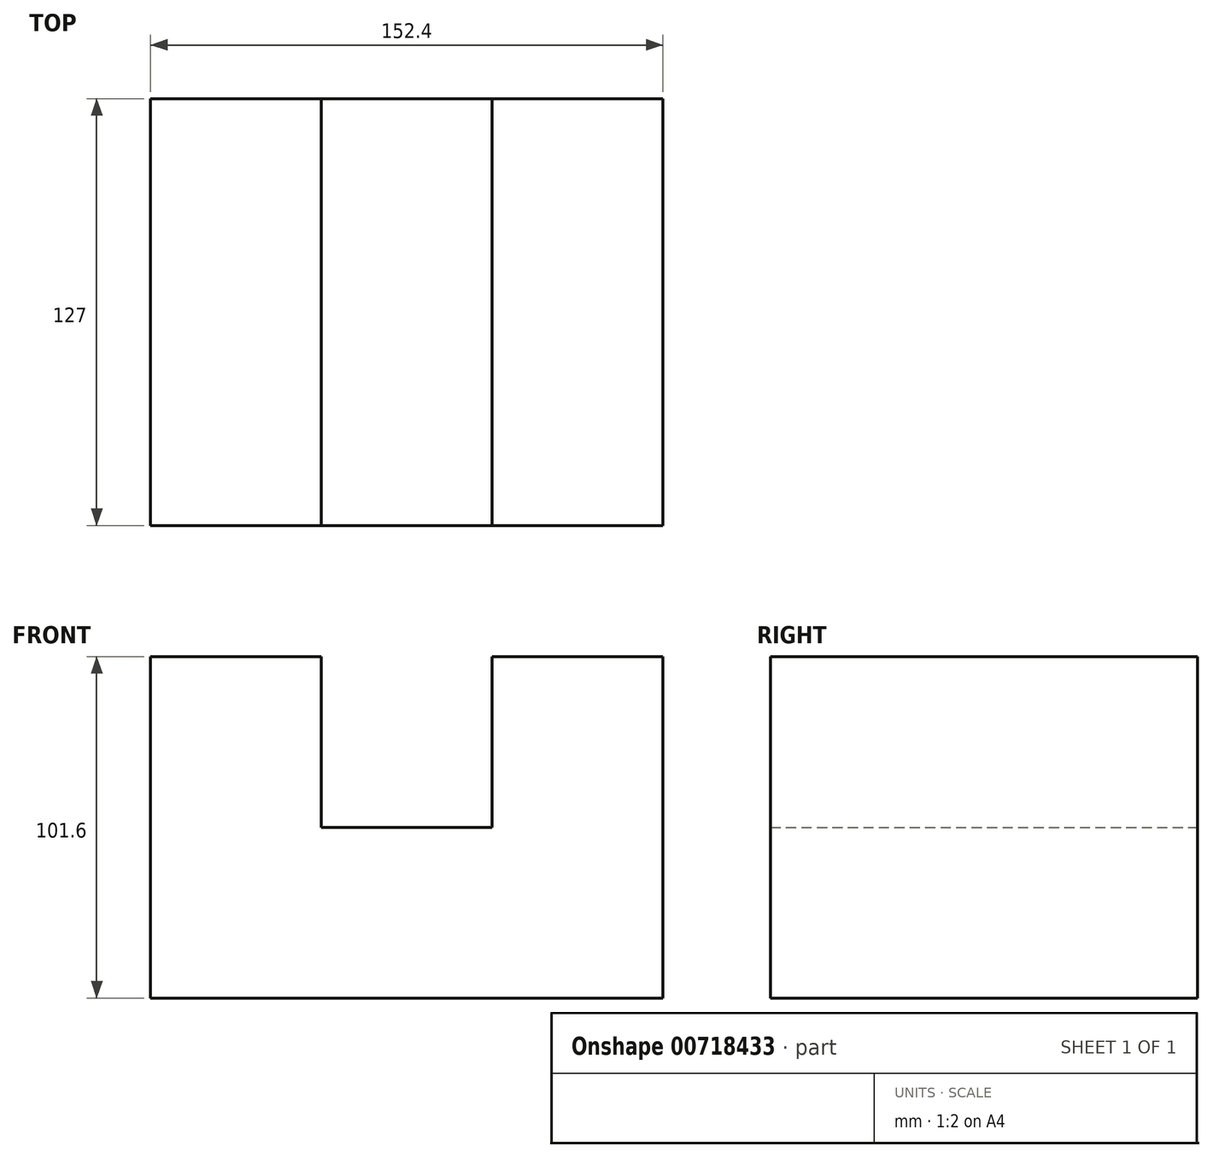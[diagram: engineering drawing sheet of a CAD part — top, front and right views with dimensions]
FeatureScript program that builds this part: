
annotation { "Feature Type Name" : "Feature", "Feature Type Description" : "" }
export const myFeature = defineFeature(function(context is Context, id is Id, definition is map)
    precondition{}
    {
        {
            var Q0;
            Q0=qCreatedBy(makeId("Front.planeOp"),FACE);
            var sketch = newSketch(context, id + "F0", { "sketchPlane" : qUnion([Q0])});
            skLineSegment(sketch, "E0", {"start": v(-76.07, -54.73) * mm, "end": v(76.33, -54.73) * mm});
            skLineSegment(sketch, "E1", {"start": v(76.33, -54.73) * mm, "end": v(76.33, 46.87) * mm});
            skLineSegment(sketch, "E2", {"start": v(76.33, 46.87) * mm, "end": v(25.53, 46.87) * mm});
            skLineSegment(sketch, "E3", {"start": v(25.53, 46.87) * mm, "end": v(25.53, -3.93) * mm});
            skLineSegment(sketch, "E4", {"start": v(25.53, -3.93) * mm, "end": v(-25.27, -3.93) * mm});
            skLineSegment(sketch, "E5", {"start": v(-25.27, -3.93) * mm, "end": v(-25.27, 46.87) * mm});
            skLineSegment(sketch, "E6", {"start": v(-25.27, 46.87) * mm, "end": v(-76.07, 46.87) * mm});
            skLineSegment(sketch, "E7", {"start": v(-76.07, 46.87) * mm, "end": v(-76.07, -54.73) * mm});
            skSolve(sketch);
        }
        {
            var Q0;
            Q0=makeQuery(id+"F0.imprint","IMPRINT",FACE,{"disambiguationData":[TD([[makeQuery(id+"F0.imprint","IMPRINT",EDGE,{"derivedFrom":sQuery(id+"F0.wireOp",EDGE,"E0")}),1.0]])]});
            extrude(context, id + "F1", {"entities" : qUnion([Q0]), "depth" : 127 * mm, "offsetDistance" : 25.4 * mm});
        }
    });
